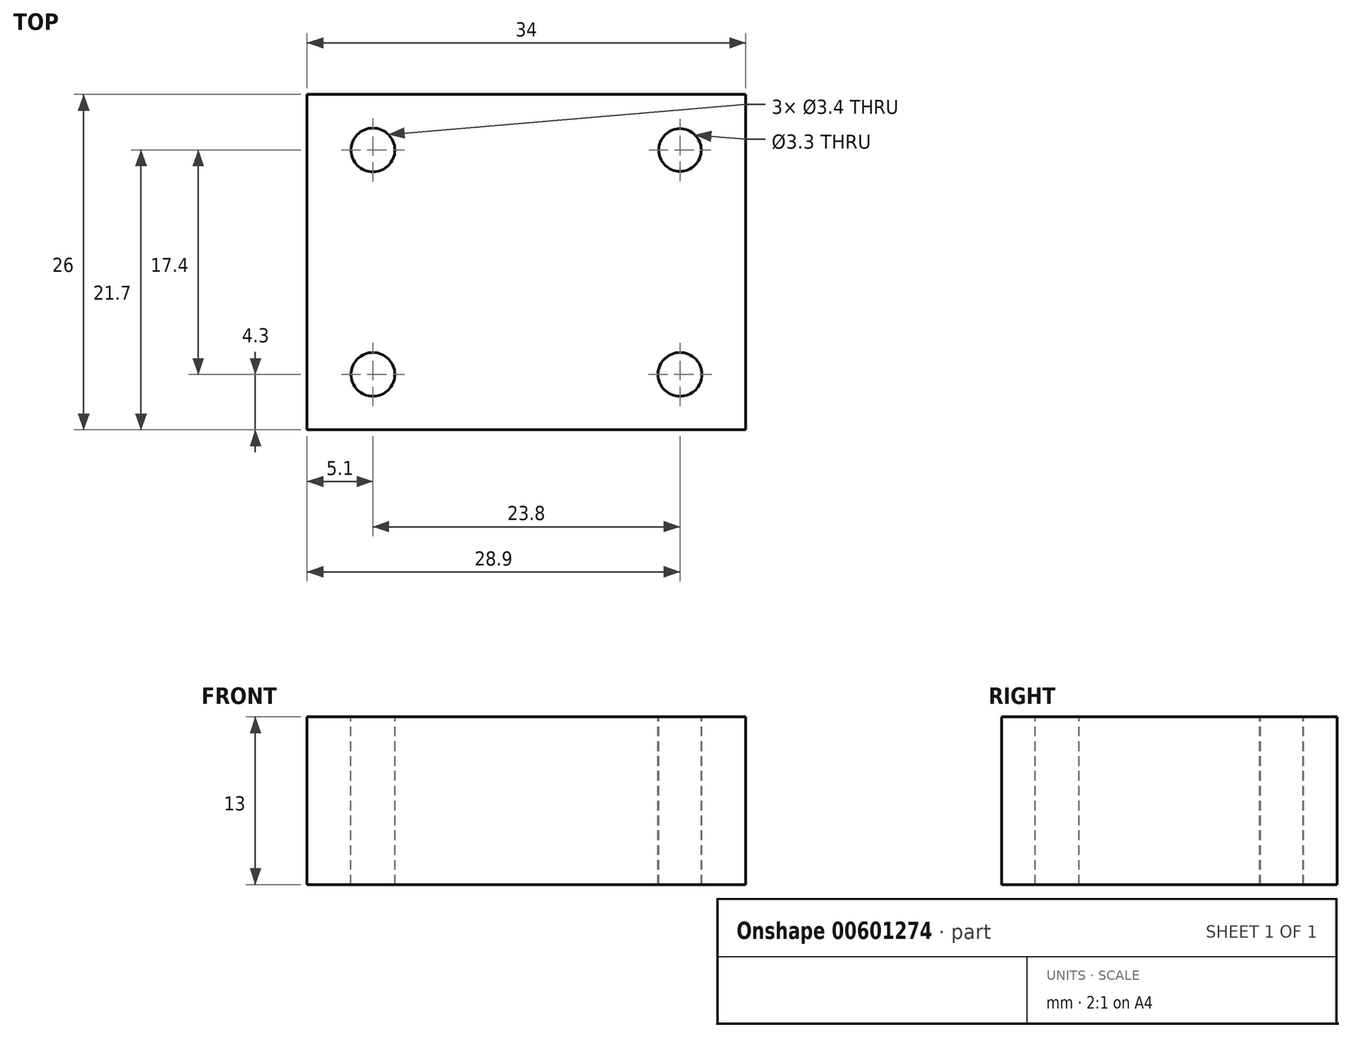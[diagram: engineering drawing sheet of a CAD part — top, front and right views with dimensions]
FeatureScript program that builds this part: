
annotation { "Feature Type Name" : "Feature", "Feature Type Description" : "" }
export const myFeature = defineFeature(function(context is Context, id is Id, definition is map)
    precondition{}
    {
        {
            var Q0;
            Q0=qCreatedBy(makeId("Top.planeOp"),FACE);
            var sketch = newSketch(context, id + "F0", { "sketchPlane" : qUnion([Q0])});
            skLineSegment(sketch, "E0.bottom", {"start": v(0, 0) * mm, "end": v(34, 0) * mm});
            skLineSegment(sketch, "E0.top", {"start": v(0, 26) * mm, "end": v(34, 26) * mm});
            skLineSegment(sketch, "E0.left", {"start": v(0, 0) * mm, "end": v(0, 26) * mm});
            skLineSegment(sketch, "E0.right", {"start": v(34, 0) * mm, "end": v(34, 26) * mm});
            skSolve(sketch);
        }
        {
            var Q0;
            Q0 = qSketchRegion(id + "F0", true);
            extrude(context, id + "F1", {"entities" : qUnion([Q0]), "depth" : 13 * mm, "offsetDistance" : 25 * mm});
        }
        {
            var Q0;
            Q0=makeQuery(id+"F1.opExtrude","CAP_FACE",FACE,{"disambiguationData":[OSD([sQuery(id+"F0.wireOp",EDGE,"E0.bottom"),sQuery(id+"F0.wireOp",EDGE,"E0.top"),sQuery(id+"F0.wireOp",EDGE,"E0.left"),sQuery(id+"F0.wireOp",EDGE,"E0.right")])],"isStart":false});
            var sketch = newSketch(context, id + "F2", { "sketchPlane" : qUnion([Q0])});
            skLineSegment(sketch, "E1.bottom", {"start": v(0, 0) * mm, "end": v(5.1, 0) * mm});
            skLineSegment(sketch, "E1.top", {"start": v(0, 4.3) * mm, "end": v(5.1, 4.3) * mm});
            skLineSegment(sketch, "E1.left", {"start": v(0, 0) * mm, "end": v(0, 4.3) * mm});
            skLineSegment(sketch, "E1.right", {"start": v(5.1, 0) * mm, "end": v(5.1, 4.3) * mm});
            skLineSegment(sketch, "E2.bottom", {"start": v(0, 26) * mm, "end": v(5.1, 26) * mm});
            skLineSegment(sketch, "E2.top", {"start": v(0, 21.7) * mm, "end": v(5.1, 21.7) * mm});
            skLineSegment(sketch, "E2.left", {"start": v(0, 26) * mm, "end": v(0, 21.7) * mm});
            skLineSegment(sketch, "E2.right", {"start": v(5.1, 26) * mm, "end": v(5.1, 21.7) * mm});
            skLineSegment(sketch, "E3.bottom", {"start": v(34, 26) * mm, "end": v(28.9, 26) * mm});
            skLineSegment(sketch, "E3.top", {"start": v(34, 21.7) * mm, "end": v(28.9, 21.7) * mm});
            skLineSegment(sketch, "E3.left", {"start": v(34, 26) * mm, "end": v(34, 21.7) * mm});
            skLineSegment(sketch, "E3.right", {"start": v(28.9, 26) * mm, "end": v(28.9, 21.7) * mm});
            skLineSegment(sketch, "E4.bottom", {"start": v(34, 0) * mm, "end": v(28.9, 0) * mm});
            skLineSegment(sketch, "E4.top", {"start": v(34, 4.3) * mm, "end": v(28.9, 4.3) * mm});
            skLineSegment(sketch, "E4.left", {"start": v(34, 0) * mm, "end": v(34, 4.3) * mm});
            skLineSegment(sketch, "E4.right", {"start": v(28.9, 0) * mm, "end": v(28.9, 4.3) * mm});
            skCircle(sketch, "E5", {"center": v(28.9, 21.7) * mm, "radius": 1.65 * mm});
            skCircle(sketch, "E6", {"center": v(5.1, 21.7) * mm, "radius": 1.7 * mm});
            skCircle(sketch, "E7", {"center": v(28.9, 4.3) * mm, "radius": 1.7 * mm});
            skCircle(sketch, "E8", {"center": v(5.1, 4.3) * mm, "radius": 1.7 * mm});
            skSolve(sketch);
        }
        {
            var Q0;
            {var subQ0=sQuery(id+"F2.wireOp",EDGE,"E2.right");var subQ1=sQuery(id+"F2.wireOp",EDGE,"E2.top");var subQ2=makeQuery(id+"F2.imprint","INTERSECT",VERTEX,{"derivedFrom":[subQ1,subQ0]});Q0=makeQuery(id+"F2.imprint","IMPRINT",FACE,{"disambiguationData":[TD([[makeQuery(id+"F2.imprint","IMPRINT",EDGE,{"disambiguationData":[TD([[subQ2,1.0]])],"derivedFrom":subQ1}),-1.0]])]});}
            var Q1;
            {var subQ0=sQuery(id+"F2.wireOp",EDGE,"E3.right");var subQ1=sQuery(id+"F2.wireOp",EDGE,"E3.top");var subQ2=makeQuery(id+"F2.imprint","INTERSECT",VERTEX,{"derivedFrom":[subQ1,subQ0]});Q1=makeQuery(id+"F2.imprint","IMPRINT",FACE,{"disambiguationData":[TD([[makeQuery(id+"F2.imprint","IMPRINT",EDGE,{"disambiguationData":[TD([[subQ2,1.0]])],"derivedFrom":subQ1}),1.0]])]});}
            var Q2;
            {var subQ0=sQuery(id+"F2.wireOp",EDGE,"E4.right");var subQ1=sQuery(id+"F2.wireOp",EDGE,"E4.top");var subQ2=makeQuery(id+"F2.imprint","INTERSECT",VERTEX,{"derivedFrom":[subQ1,subQ0]});Q2=makeQuery(id+"F2.imprint","IMPRINT",FACE,{"disambiguationData":[TD([[makeQuery(id+"F2.imprint","IMPRINT",EDGE,{"disambiguationData":[TD([[subQ2,1.0]])],"derivedFrom":subQ1}),-1.0]])]});}
            var Q3;
            {var subQ0=sQuery(id+"F2.wireOp",EDGE,"E1.right");var subQ1=sQuery(id+"F2.wireOp",EDGE,"E1.top");var subQ2=makeQuery(id+"F2.imprint","INTERSECT",VERTEX,{"derivedFrom":[subQ1,subQ0]});Q3=makeQuery(id+"F2.imprint","IMPRINT",FACE,{"disambiguationData":[TD([[makeQuery(id+"F2.imprint","IMPRINT",EDGE,{"disambiguationData":[TD([[subQ2,1.0]])],"derivedFrom":subQ1}),1.0]])]});}
            var Q4;
            {var subQ0=sQuery(id+"F2.wireOp",EDGE,"E1.right");var subQ1=sQuery(id+"F2.wireOp",EDGE,"E1.top");var subQ2=makeQuery(id+"F2.imprint","INTERSECT",VERTEX,{"derivedFrom":[subQ1,subQ0]});Q4=makeQuery(id+"F2.imprint","IMPRINT",FACE,{"disambiguationData":[TD([[makeQuery(id+"F2.imprint","IMPRINT",EDGE,{"disambiguationData":[TD([[subQ2,1.0]])],"derivedFrom":subQ1}),-1.0]])]});}
            var Q5;
            {var subQ0=sQuery(id+"F2.wireOp",EDGE,"E4.right");var subQ1=sQuery(id+"F2.wireOp",EDGE,"E4.top");var subQ2=makeQuery(id+"F2.imprint","INTERSECT",VERTEX,{"derivedFrom":[subQ1,subQ0]});Q5=makeQuery(id+"F2.imprint","IMPRINT",FACE,{"disambiguationData":[TD([[makeQuery(id+"F2.imprint","IMPRINT",EDGE,{"disambiguationData":[TD([[subQ2,1.0]])],"derivedFrom":subQ1}),1.0]])]});}
            var Q6;
            {var subQ0=sQuery(id+"F2.wireOp",EDGE,"E3.right");var subQ1=sQuery(id+"F2.wireOp",EDGE,"E3.top");var subQ2=makeQuery(id+"F2.imprint","INTERSECT",VERTEX,{"derivedFrom":[subQ1,subQ0]});Q6=makeQuery(id+"F2.imprint","IMPRINT",FACE,{"disambiguationData":[TD([[makeQuery(id+"F2.imprint","IMPRINT",EDGE,{"disambiguationData":[TD([[subQ2,1.0]])],"derivedFrom":subQ1}),-1.0]])]});}
            var Q7;
            {var subQ0=sQuery(id+"F2.wireOp",EDGE,"E2.right");var subQ1=sQuery(id+"F2.wireOp",EDGE,"E2.top");var subQ2=makeQuery(id+"F2.imprint","INTERSECT",VERTEX,{"derivedFrom":[subQ1,subQ0]});Q7=makeQuery(id+"F2.imprint","IMPRINT",FACE,{"disambiguationData":[TD([[makeQuery(id+"F2.imprint","IMPRINT",EDGE,{"disambiguationData":[TD([[subQ2,1.0]])],"derivedFrom":subQ1}),1.0]])]});}
            extrude(context, id + "F3", {"entities" : qUnion([Q0, Q1, Q2, Q3, Q4, Q5, Q6, Q7]), "operationType" : NewBodyOperationType.REMOVE, "oppositeDirection" : true, "depth" : 25 * mm, "offsetDistance" : 25 * mm});
        }
    });
